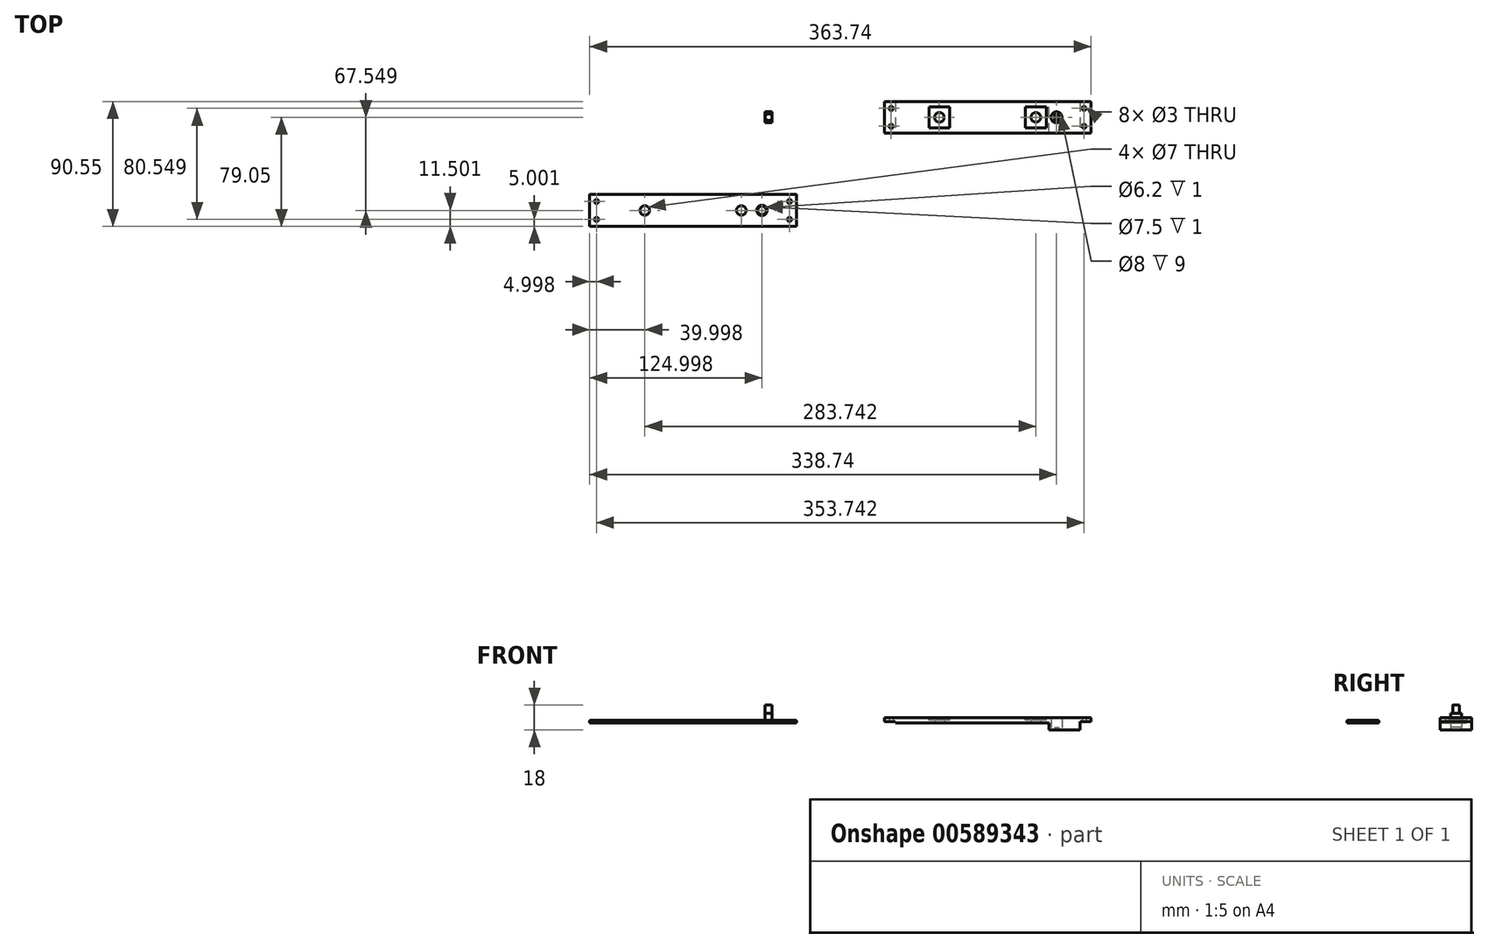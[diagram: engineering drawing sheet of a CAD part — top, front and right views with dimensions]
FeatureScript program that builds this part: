
annotation { "Feature Type Name" : "Feature", "Feature Type Description" : "" }
export const myFeature = defineFeature(function(context is Context, id is Id, definition is map)
    precondition{}
    {
        {
            var Q0;
            Q0=qCreatedBy(makeId("Top.planeOp"),FACE);
            var sketch = newSketch(context, id + "F0", { "sketchPlane" : qUnion([Q0])});
            skLineSegment(sketch, "E0.bottom", {"start": v(75, -11.5) * mm, "end": v(-75, -11.5) * mm});
            skLineSegment(sketch, "E0.top", {"start": v(75, 11.5) * mm, "end": v(-75, 11.5) * mm});
            skLineSegment(sketch, "E0.left", {"start": v(75, -11.5) * mm, "end": v(75, 11.5) * mm});
            skLineSegment(sketch, "E0.right", {"start": v(-75, -11.5) * mm, "end": v(-75, 11.5) * mm});
            skPoint(sketch, "E0.middle", {"position": v(0, 0) * mm});
            skLineSegment(sketch, "E1.bottom", {"start": v(-75, 11.5) * mm, "end": v(-67, 11.5) * mm, "construction": true});
            skLineSegment(sketch, "E1.top", {"start": v(-75, -11.5) * mm, "end": v(-67, -11.5) * mm, "construction": true});
            skLineSegment(sketch, "E1.left", {"start": v(-75, 11.5) * mm, "end": v(-75, -11.5) * mm, "construction": true});
            skLineSegment(sketch, "E1.right", {"start": v(-67, 11.5) * mm, "end": v(-67, -11.5) * mm, "construction": true});
            skLineSegment(sketch, "E2.bottom", {"start": v(75, -11.5) * mm, "end": v(67, -11.5) * mm, "construction": true});
            skLineSegment(sketch, "E2.top", {"start": v(75, 11.5) * mm, "end": v(67, 11.5) * mm, "construction": true});
            skLineSegment(sketch, "E2.left", {"start": v(75, -11.5) * mm, "end": v(75, 11.5) * mm, "construction": true});
            skLineSegment(sketch, "E2.right", {"start": v(67, -11.5) * mm, "end": v(67, 11.5) * mm, "construction": true});
            skCircle(sketch, "E3", {"center": v(-35, 0) * mm, "radius": 3.5 * mm});
            skCircle(sketch, "E4", {"center": v(35, 0) * mm, "radius": 3.5 * mm});
            skCircle(sketch, "E5", {"center": v(50, 0) * mm, "radius": 4 * mm});
            skLineSegment(sketch, "E6.left", {"start": v(51.5, -3.7) * mm, "end": v(51.5, 3.7) * mm, "construction": true});
            skLineSegment(sketch, "E6.right", {"start": v(48.5, -3.7) * mm, "end": v(48.5, 3.7) * mm, "construction": true});
            skCircle(sketch, "E7", {"center": v(-70, 6.5) * mm, "radius": 1.5 * mm});
            skCircle(sketch, "E8", {"center": v(-70, -6.5) * mm, "radius": 1.5 * mm});
            skCircle(sketch, "E9", {"center": v(70, 6.5) * mm, "radius": 1.5 * mm});
            skCircle(sketch, "E10", {"center": v(70, -6.5) * mm, "radius": 1.5 * mm});
            skSolve(sketch);
        }
        {
            var Q0;
            Q0=qCreatedBy(makeId("Top.planeOp"),FACE);
            var sketch = newSketch(context, id + "F1", { "sketchPlane" : qUnion([Q0])});
            skLineSegment(sketch, "E11.bottom", {"start": v(-156.38, -3.9) * mm, "end": v(-161.38, -3.9) * mm});
            skLineSegment(sketch, "E11.top", {"start": v(-156.38, 4.1) * mm, "end": v(-161.38, 4.1) * mm});
            skLineSegment(sketch, "E11.left", {"start": v(-156.38, -3.9) * mm, "end": v(-156.38, 4.1) * mm});
            skLineSegment(sketch, "E11.right", {"start": v(-161.38, -3.9) * mm, "end": v(-161.38, 4.1) * mm});
            skPoint(sketch, "E11.middle", {"position": v(-158.88, 0.1) * mm});
            skSolve(sketch);
        }
        {
            var Q0;
            Q0=makeQuery(id+"F1.imprint","IMPRINT",FACE,{"disambiguationData":[TD([[makeQuery(id+"F1.imprint","IMPRINT",EDGE,{"derivedFrom":sQuery(id+"F1.wireOp",EDGE,"E11.bottom")}),-1.0]])]});
            extrude(context, id + "F2", {"entities" : qUnion([Q0]), "depth" : 7 * mm});
        }
        {
            var Q0;
            Q0=makeQuery(id+"F2.opExtrude","CAP_FACE",FACE,{"disambiguationData":[OSD([sQuery(id+"F1.wireOp",EDGE,"E11.bottom"),sQuery(id+"F1.wireOp",EDGE,"E11.top"),sQuery(id+"F1.wireOp",EDGE,"E11.left"),sQuery(id+"F1.wireOp",EDGE,"E11.right")])],"isStart":false});
            var sketch = newSketch(context, id + "F3", { "sketchPlane" : qUnion([Q0])});
            skCircle(sketch, "E12", {"center": v(-158.88, 0.1) * mm, "radius": 2.5 * mm});
            skPoint(sketch, "E12.centerSnap0", {"position": v(-161.38, 0.1) * mm});
            skPoint(sketch, "E12.centerSnap1", {"position": v(-158.88, 4.1) * mm});
            skSolve(sketch);
        }
        {
            var Q0;
            {var subQ0=sQuery(id+"F3.wireOp",EDGE,"E12");var subQ1=makeQuery(id+"F3.imprint","INTERSECT",VERTEX,{"derivedFrom":[makeQuery(id+"F2.opExtrude","CAP_EDGE",EDGE,{"disambiguationData":[OSD([sQuery(id+"F1.wireOp",EDGE,"E11.left")])],"isStart":false}),subQ0]});Q0=makeQuery(id+"F3.imprint","IMPRINT",FACE,{"disambiguationData":[TD([[makeQuery(id+"F3.imprint","IMPRINT",EDGE,{"disambiguationData":[TD([[subQ1,-1.0]])],"derivedFrom":subQ0}),1.0]])]});}
            extrude(context, id + "F4", {"entities" : qUnion([Q0]), "operationType" : NewBodyOperationType.ADD, "depth" : 6 * mm});
        }
        {
            var Q0;
            Q0=makeQuery(id+"F0.imprint","IMPRINT",FACE,{"disambiguationData":[TD([[makeQuery(id+"F0.imprint","IMPRINT",EDGE,{"derivedFrom":sQuery(id+"F0.wireOp",EDGE,"E0.bottom")}),-1.0]])]});
            var Q1;
            {var subQ0=sQuery(id+"F0.wireOp",EDGE,"E6.left");Q1=makeQuery(id+"F0.imprint","IMPRINT",FACE,{"disambiguationData":[TD([[makeQuery(id+"F0.imprint","IMPRINT",EDGE,{"derivedFrom":subQ0}),1.0]])]});}
            extrude(context, id + "F5", {"entities" : qUnion([Q0, Q1]), "depth" : 4 * mm});
        }
        {
            var Q0;
            Q0=qCreatedBy(makeId("Top.planeOp"),FACE);
            var sketch = newSketch(context, id + "F6", { "sketchPlane" : qUnion([Q0])});
            skLineSegment(sketch, "E13.bottom", {"start": v(-138.74, -79.05) * mm, "end": v(-288.74, -79.05) * mm});
            skLineSegment(sketch, "E13.top", {"start": v(-138.74, -56.05) * mm, "end": v(-288.74, -56.05) * mm});
            skLineSegment(sketch, "E13.left", {"start": v(-138.74, -79.05) * mm, "end": v(-138.74, -56.05) * mm});
            skLineSegment(sketch, "E13.right", {"start": v(-288.74, -79.05) * mm, "end": v(-288.74, -56.05) * mm});
            skPoint(sketch, "E13.middle", {"position": v(-213.74, -67.55) * mm});
            skLineSegment(sketch, "E14.bottom", {"start": v(-288.74, -56.05) * mm, "end": v(-280.74, -56.05) * mm, "construction": true});
            skLineSegment(sketch, "E14.top", {"start": v(-288.74, -79.05) * mm, "end": v(-280.74, -79.05) * mm, "construction": true});
            skLineSegment(sketch, "E14.left", {"start": v(-288.74, -56.05) * mm, "end": v(-288.74, -79.05) * mm, "construction": true});
            skLineSegment(sketch, "E14.right", {"start": v(-280.74, -56.05) * mm, "end": v(-280.74, -79.05) * mm, "construction": true});
            skLineSegment(sketch, "E15.bottom", {"start": v(-138.74, -79.05) * mm, "end": v(-146.74, -79.05) * mm, "construction": true});
            skLineSegment(sketch, "E15.top", {"start": v(-138.74, -56.05) * mm, "end": v(-146.74, -56.05) * mm, "construction": true});
            skLineSegment(sketch, "E15.left", {"start": v(-138.74, -79.05) * mm, "end": v(-138.74, -56.05) * mm, "construction": true});
            skLineSegment(sketch, "E15.right", {"start": v(-146.74, -79.05) * mm, "end": v(-146.74, -56.05) * mm, "construction": true});
            skCircle(sketch, "E16", {"center": v(-248.74, -67.55) * mm, "radius": 3.5 * mm});
            skCircle(sketch, "E17", {"center": v(-178.74, -67.55) * mm, "radius": 3.5 * mm});
            skCircle(sketch, "E18", {"center": v(-163.74, -67.55) * mm, "radius": 3.1 * mm});
            skCircle(sketch, "E19", {"center": v(-283.74, -61.05) * mm, "radius": 1.5 * mm});
            skCircle(sketch, "E20", {"center": v(-283.74, -74.05) * mm, "radius": 1.5 * mm});
            skCircle(sketch, "E21", {"center": v(-143.74, -61.05) * mm, "radius": 1.5 * mm});
            skCircle(sketch, "E22", {"center": v(-143.74, -74.05) * mm, "radius": 1.5 * mm});
            skSolve(sketch);
        }
        {
            var Q0;
            Q0=makeQuery(id+"F6.imprint","IMPRINT",FACE,{"disambiguationData":[TD([[makeQuery(id+"F6.imprint","IMPRINT",EDGE,{"derivedFrom":sQuery(id+"F6.wireOp",EDGE,"E13.bottom")}),-1.0]])]});
            extrude(context, id + "F7", {"entities" : qUnion([Q0]), "depth" : 2 * mm});
        }
        {
            var Q0;
            Q0=makeQuery(id+"F7.opExtrude","CAP_FACE",FACE,{"disambiguationData":[OSD([sQuery(id+"F6.wireOp",EDGE,"E13.bottom"),sQuery(id+"F6.wireOp",EDGE,"E13.top"),sQuery(id+"F6.wireOp",EDGE,"E13.left"),sQuery(id+"F6.wireOp",EDGE,"E13.right"),sQuery(id+"F6.wireOp",EDGE,"E16"),sQuery(id+"F6.wireOp",EDGE,"E17"),sQuery(id+"F6.wireOp",EDGE,"E18")])],"isStart":false});
            var sketch = newSketch(context, id + "F8", { "sketchPlane" : qUnion([Q0])});
            skCircle(sketch, "E23", {"center": v(-163.74, -67.55) * mm, "radius": 3.75 * mm});
            skSolve(sketch);
        }
        {
            var Q0;
            Q0=qSketchRegion(id+"F8",true);
            extrude(context, id + "F9", {"entities" : qUnion([Q0]), "operationType" : NewBodyOperationType.REMOVE, "oppositeDirection" : true, "depth" : 1 * mm});
        }
        {
            var Q0;
            Q0=makeQuery(id+"F5.opExtrude","SWEPT_FACE",FACE,{"disambiguationData":[OSD([sQuery(id+"F0.wireOp",EDGE,"E0.bottom")])]});
            var sketch = newSketch(context, id + "F10", { "sketchPlane" : qUnion([Q0])});
            skLineSegment(sketch, "E24.bottom", {"start": v(-75, 0) * mm, "end": v(-67, 0) * mm});
            skLineSegment(sketch, "E24.top", {"start": v(-75, 1) * mm, "end": v(-67, 1) * mm});
            skLineSegment(sketch, "E24.left", {"start": v(-75, 0) * mm, "end": v(-75, 1) * mm});
            skLineSegment(sketch, "E24.right", {"start": v(-67, 0) * mm, "end": v(-67, 1) * mm});
            skLineSegment(sketch, "E25.bottom", {"start": v(75, 0) * mm, "end": v(67, 0) * mm});
            skLineSegment(sketch, "E25.top", {"start": v(75, 1) * mm, "end": v(67, 1) * mm});
            skLineSegment(sketch, "E25.left", {"start": v(75, 0) * mm, "end": v(75, 1) * mm});
            skLineSegment(sketch, "E25.right", {"start": v(67, 0) * mm, "end": v(67, 1) * mm});
            skSolve(sketch);
        }
        {
            var Q0;
            Q0=qSketchRegion(id+"F10",true);
            extrude(context, id + "F11", {"entities" : qUnion([Q0]), "operationType" : NewBodyOperationType.REMOVE, "oppositeDirection" : true, "depth" : 30 * mm});
        }
        {
            var Q0;
            Q0=makeQuery(id+"F5.opExtrude","CAP_FACE",FACE,{"disambiguationData":[OSD([sQuery(id+"F0.wireOp",EDGE,"E0.bottom"),sQuery(id+"F0.wireOp",EDGE,"E0.top"),sQuery(id+"F0.wireOp",EDGE,"E0.left"),sQuery(id+"F0.wireOp",EDGE,"E0.right"),sQuery(id+"F0.wireOp",EDGE,"E3"),sQuery(id+"F0.wireOp",EDGE,"E4"),sQuery(id+"F0.wireOp",EDGE,"E5")])],"isStart":false});
            var sketch = newSketch(context, id + "F12", { "sketchPlane" : qUnion([Q0])});
            skLineSegment(sketch, "E26.bottom", {"start": v(-27.5, -7.5) * mm, "end": v(-42.5, -7.5) * mm});
            skLineSegment(sketch, "E26.top", {"start": v(-27.5, 7.5) * mm, "end": v(-42.5, 7.5) * mm});
            skLineSegment(sketch, "E26.left", {"start": v(-27.5, -7.5) * mm, "end": v(-27.5, 7.5) * mm});
            skLineSegment(sketch, "E26.right", {"start": v(-42.5, -7.5) * mm, "end": v(-42.5, 7.5) * mm});
            skPoint(sketch, "E26.middle", {"position": v(-35, 0) * mm});
            skLineSegment(sketch, "E27.bottom", {"start": v(42.5, -7.5) * mm, "end": v(27.5, -7.5) * mm});
            skLineSegment(sketch, "E27.top", {"start": v(42.5, 7.5) * mm, "end": v(27.5, 7.5) * mm});
            skLineSegment(sketch, "E27.left", {"start": v(42.5, -7.5) * mm, "end": v(42.5, 7.5) * mm});
            skLineSegment(sketch, "E27.right", {"start": v(27.5, -7.5) * mm, "end": v(27.5, 7.5) * mm});
            skPoint(sketch, "E27.middle", {"position": v(35, 0) * mm});
            skSolve(sketch);
        }
        {
            var Q0;
            Q0=makeQuery(id+"F12.imprint","IMPRINT",FACE,{"disambiguationData":[TD([[makeQuery(id+"F12.imprint","IMPRINT",EDGE,{"derivedFrom":sQuery(id+"F12.wireOp",EDGE,"E26.bottom")}),-1.0]])]});
            var Q1;
            Q1=makeQuery(id+"F12.imprint","IMPRINT",FACE,{"disambiguationData":[TD([[makeQuery(id+"F12.imprint","IMPRINT",EDGE,{"derivedFrom":sQuery(id+"F12.wireOp",EDGE,"E27.bottom")}),-1.0]])]});
            extrude(context, id + "F13", {"entities" : qUnion([Q0, Q1]), "operationType" : NewBodyOperationType.REMOVE, "oppositeDirection" : true, "depth" : 2 * mm});
        }
        {
            var Q0;
            Q0=makeQuery(id+"F5.opExtrude","CAP_FACE",FACE,{"disambiguationData":[OSD([sQuery(id+"F0.wireOp",EDGE,"E0.bottom"),sQuery(id+"F0.wireOp",EDGE,"E0.top"),sQuery(id+"F0.wireOp",EDGE,"E0.left"),sQuery(id+"F0.wireOp",EDGE,"E0.right"),sQuery(id+"F0.wireOp",EDGE,"E3"),sQuery(id+"F0.wireOp",EDGE,"E4"),sQuery(id+"F0.wireOp",EDGE,"E5"),sQuery(id+"F0.wireOp",EDGE,"E6.left"),sQuery(id+"F0.wireOp",EDGE,"E6.right")])],"isStart":false});
            var sketch = newSketch(context, id + "F14", { "sketchPlane" : qUnion([Q0])});
            skCircle(sketch, "E28", {"center": v(50, 0) * mm, "radius": 4 * mm});
            skSolve(sketch);
        }
        {
            var Q0;
            Q0=qSketchRegion(id+"F14",true);
            extrude(context, id + "F15", {"entities" : qUnion([Q0]), "operationType" : NewBodyOperationType.REMOVE, "oppositeDirection" : true, "depth" : 3 * mm});
        }
        {
            var Q0;
            Q0=makeQuery(id+"F0.imprint","IMPRINT",FACE,{"disambiguationData":[TD([[makeQuery(id+"F0.imprint","IMPRINT",EDGE,{"derivedFrom":sQuery(id+"F0.wireOp",EDGE,"E0.bottom")}),-1.0]])]});
            var sketch = newSketch(context, id + "F16", { "sketchPlane" : qUnion([Q0])});
            skPoint(sketch, "E29.0", {"position": v(67, -11.5) * mm});
            skPoint(sketch, "E29.1", {"position": v(67, 11.5) * mm});
            skLineSegment(sketch, "E30.bottom", {"start": v(67, -11.5) * mm, "end": v(44.5, -11.5) * mm});
            skLineSegment(sketch, "E30.top", {"start": v(67, 11.5) * mm, "end": v(44.5, 11.5) * mm});
            skLineSegment(sketch, "E30.left", {"start": v(67, -11.5) * mm, "end": v(67, 11.5) * mm});
            skLineSegment(sketch, "E30.right", {"start": v(44.5, -11.5) * mm, "end": v(44.5, 11.5) * mm});
            skCircle(sketch, "E31", {"center": v(50, 0) * mm, "radius": 4 * mm});
            skSolve(sketch);
        }
        {
            var Q0;
            Q0=makeQuery(id+"F7.opExtrude","CAP_EDGE",EDGE,{"disambiguationData":[OSD([sQuery(id+"F6.wireOp",EDGE,"E13.right")])],"isStart":false});
            var Q1;
            Q1=makeQuery(id+"F7.opExtrude","CAP_EDGE",EDGE,{"disambiguationData":[OSD([sQuery(id+"F6.wireOp",EDGE,"E13.top")])],"isStart":false});
            var Q2;
            Q2=makeQuery(id+"F7.opExtrude","CAP_EDGE",EDGE,{"disambiguationData":[OSD([sQuery(id+"F6.wireOp",EDGE,"E13.bottom")])],"isStart":false});
            var Q3;
            Q3=makeQuery(id+"F7.opExtrude","CAP_EDGE",EDGE,{"disambiguationData":[OSD([sQuery(id+"F6.wireOp",EDGE,"E13.left")])],"isStart":false});
            fillet(context, id + "F17", {"entities" : qUnion([Q0, Q1, Q2, Q3]), "radius" : 0.5 * mm, "tangentPropagation" : true, "allowEdgeOverflow" : false});
        }
        {
            var Q0;
            Q0=qSketchRegion(id+"F16",true);
            extrude(context, id + "F18", {"entities" : qUnion([Q0]), "operationType" : NewBodyOperationType.ADD, "oppositeDirection" : true, "depth" : 5 * mm, "offsetDistance" : 25 * mm});
        }
        {
            var Q0;
            Q0=makeQuery(id+"F18.opExtrude","CAP_FACE",FACE,{"disambiguationData":[OSD([sQuery(id+"F16.wireOp",EDGE,"E30.bottom"),sQuery(id+"F16.wireOp",EDGE,"E30.top"),sQuery(id+"F16.wireOp",EDGE,"E30.left"),sQuery(id+"F16.wireOp",EDGE,"E30.right"),sQuery(id+"F16.wireOp",EDGE,"E31")])],"isStart":false});
            var sketch = newSketch(context, id + "F19", { "sketchPlane" : qUnion([Q0])});
            skPoint(sketch, "E32.0", {"position": v(50, 0) * mm});
            skLineSegment(sketch, "E33.bottom", {"start": v(51.5, -3.7) * mm, "end": v(48.5, -3.7) * mm});
            skLineSegment(sketch, "E33.top", {"start": v(51.5, 3.7) * mm, "end": v(48.5, 3.7) * mm});
            skLineSegment(sketch, "E33.left", {"start": v(51.5, -3.7) * mm, "end": v(51.5, 3.7) * mm});
            skLineSegment(sketch, "E33.right", {"start": v(48.5, -3.7) * mm, "end": v(48.5, 3.7) * mm});
            skSolve(sketch);
        }
        {
            var Q0;
            Q0=makeQuery(id+"F19.imprint","IMPRINT",FACE,{"disambiguationData":[TD([[makeQuery(id+"F19.imprint","IMPRINT",EDGE,{"derivedFrom":sQuery(id+"F19.wireOp",EDGE,"E33.bottom")}),-1.0]])]});
            var Q1;
            {var subQ0=sQuery(id+"F19.wireOp",EDGE,"E33.top");Q1=makeQuery(id+"F19.imprint","IMPRINT",FACE,{"disambiguationData":[TD([[makeQuery(id+"F19.imprint","IMPRINT",EDGE,{"derivedFrom":subQ0}),-1.0]])]});}
            var Q2;
            {var subQ0=sQuery(id+"F19.wireOp",EDGE,"E33.bottom");Q2=makeQuery(id+"F19.imprint","IMPRINT",FACE,{"disambiguationData":[TD([[makeQuery(id+"F19.imprint","IMPRINT",EDGE,{"derivedFrom":subQ0}),1.0]])]});}
            extrude(context, id + "F20", {"entities" : qUnion([Q0, Q1, Q2]), "operationType" : NewBodyOperationType.ADD, "oppositeDirection" : true, "depth" : 2 * mm, "offsetDistance" : 25 * mm});
        }
    });
